# Revit family: Faucet-Wall_Mount-Lavatory-KOHLER-Memoirs-K-T11838_1
name_source: partatom
category: Plumbing Fixtures
revit_build: Autodesk Revit 2015 (Build: 20140606_1530(x64)
units: mm (PartAtom-declared; Revit-internal decimal feet)

## types (2) — shared parameters
ADA Compliant = Yes
Assembly Code = D2010
CW Connection = Yes
Cold Water Inlet = Cold Water Inlet
Date Modified = 02/14/2019
Default Elevation = 36"
Description = Stately Wall-Mount Commercial Bathroom Sink Faucet With 8-3/16 Inch Spout And Insight Technology
Distance Of Sensor = 4 1/16"
Drain Included = No
Faucet Hole Spacing = 0"
Flow Rate = 1 GPM
HW Connection = No
Handle Clearance = 0"
Height = 1 7/8"
Hot Water Inlet = Hot Water Inlet
Length = 8 3/16"
Manufacturer = KOHLER Co.
MasterFormat 1995 = 15410
MasterFormat 2004 = 22.41.39
Material = Brass construction
Pressure = 0.00 psi
Product Documentation Link = https://www.us.kohler.com
Product Name = Memoirs
Product Page URL = http://www.us.kohler.com
Spout Reach = 8 3/16"
URL = https://www.us.kohler.com
Vent Connection = No
Waste Connection = No
Waste Water Outlet = Waste Water Outlet
WaterSense Certified = No
Width = 1 7/8"

## per-type parameters (varying)
| type | Finish | Model | Type |
| CP- Polished Chrome | Kohler-Metal-CP-Polished_Chrome | K-T11838-CP | 1 |
| VS- Vibrant Stainless | Kohler-Metal-VS-Vibrant_Stainless | K-T11838-VS | 2 |

## geometry (parser evidence)
native form markers: Sweep x7
no freeform markers — native parametric forms only
